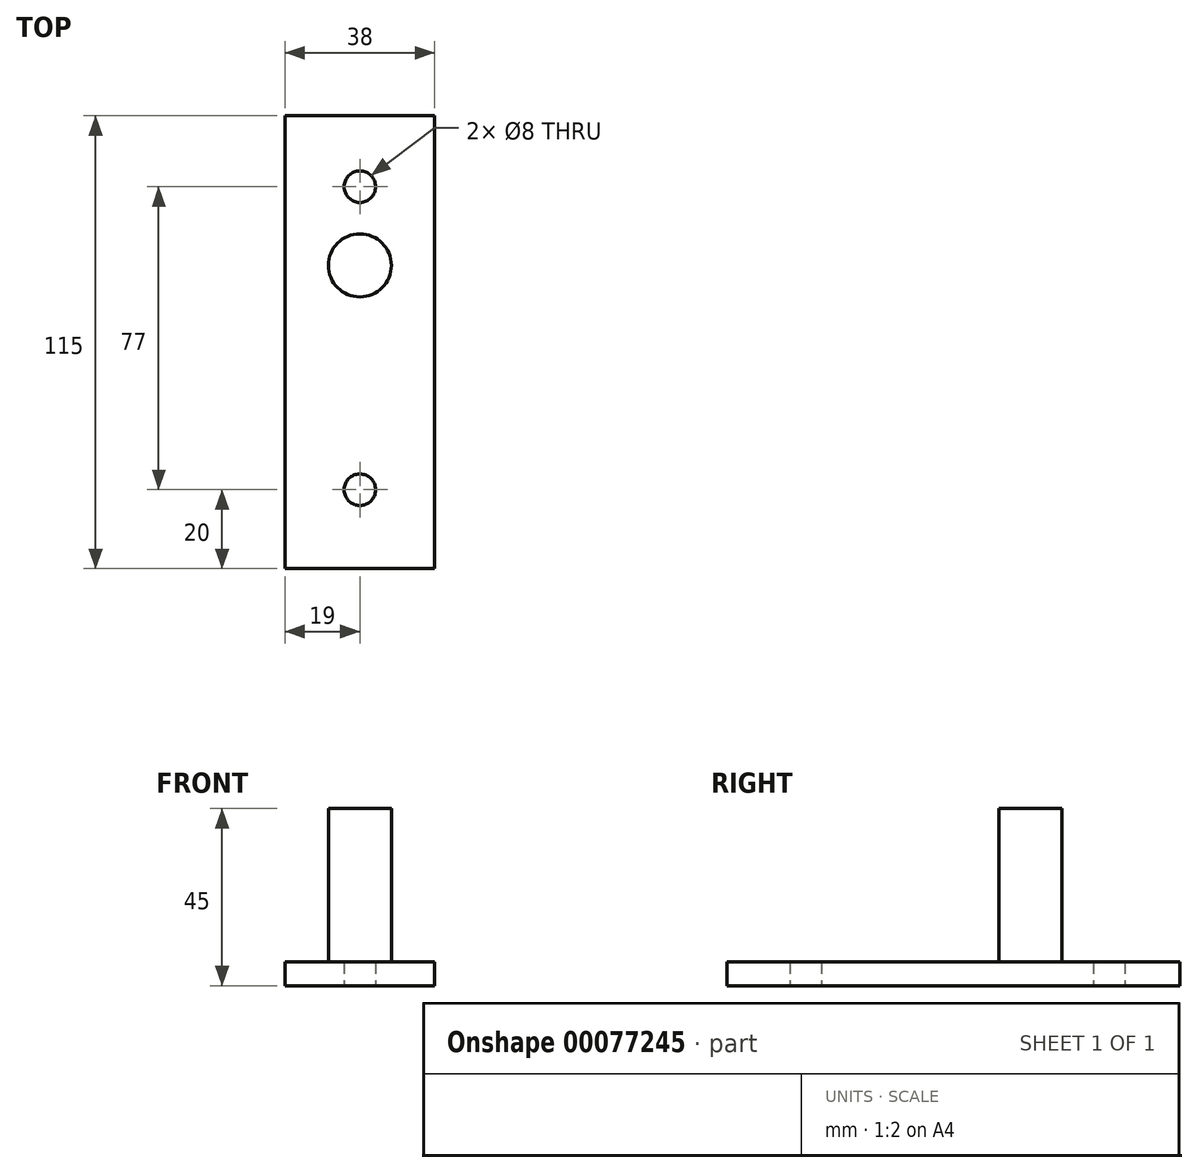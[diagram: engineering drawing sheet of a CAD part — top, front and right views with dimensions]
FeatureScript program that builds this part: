
annotation { "Feature Type Name" : "Feature", "Feature Type Description" : "" }
export const myFeature = defineFeature(function(context is Context, id is Id, definition is map)
    precondition{}
    {
        {
            var Q0;
            Q0=qCreatedBy(makeId("Top.planeOp"),FACE);
            var sketch = newSketch(context, id + "F0", { "sketchPlane" : qUnion([Q0])});
            skLineSegment(sketch, "E0", {"start": v(0, 57.5) * mm, "end": v(19, 57.5) * mm});
            skLineSegment(sketch, "E1", {"start": v(19, 57.5) * mm, "end": v(19, 0) * mm});
            skLineSegment(sketch, "E2.MirrorCS", {"start": v(0, 57.5) * mm, "end": v(-19, 57.5) * mm});
            skLineSegment(sketch, "E3.MirrorCS", {"start": v(-19, 57.5) * mm, "end": v(-19, 0) * mm});
            skLineSegment(sketch, "E4.MirrorCS", {"start": v(-19, -57.5) * mm, "end": v(-19, 0) * mm});
            skLineSegment(sketch, "E5.MirrorCS", {"start": v(19, -57.5) * mm, "end": v(19, 0) * mm});
            skLineSegment(sketch, "E6.MirrorCS", {"start": v(0, -57.5) * mm, "end": v(19, -57.5) * mm});
            skLineSegment(sketch, "E7.MirrorCS", {"start": v(0, -57.5) * mm, "end": v(-19, -57.5) * mm});
            skCircle(sketch, "E8", {"center": v(0, 19.5) * mm, "radius": 8 * mm});
            skPoint(sketch, "E9", {"position": v(0, 39.5) * mm});
            skPoint(sketch, "E10", {"position": v(0, -37.5) * mm});
            skSolve(sketch);
        }
        {
            var Q0;
            Q0 = qSketchRegion(id + "F0", true);
            var Q1;
            Q1=makeQuery(id+"F0.imprint","IMPRINT",FACE,{"disambiguationData":[TD([[makeQuery(id+"F0.imprint","IMPRINT",EDGE,{"derivedFrom":sQuery(id+"F0.wireOp",EDGE,"E8")}),1.0]])]});
            extrude(context, id + "F1", {"entities" : qUnion([Q0, Q1]), "depth" : 6 * mm});
        }
        {
            var Q0;
            Q0=makeQuery(id+"F0.imprint","IMPRINT",FACE,{"disambiguationData":[TD([[makeQuery(id+"F0.imprint","IMPRINT",EDGE,{"derivedFrom":sQuery(id+"F0.wireOp",EDGE,"E8")}),1.0]])]});
            extrude(context, id + "F2", {"entities" : qUnion([Q0]), "operationType" : NewBodyOperationType.ADD, "depth" : 45 * mm});
        }
        {
            var Q0;
            Q0=sQuery(id+"F0.wireOp",VERTEX,"E9");
            var Q1;
            Q1=sQuery(id+"F0.wireOp",VERTEX,"E10");
            var Q2;
            Q2=makeQuery(id+"F1.opExtrude","SWEPT_BODY",BODY,{"disambiguationData":[OSD([sQuery(id+"F0.wireOp",EDGE,"E0"),sQuery(id+"F0.wireOp",EDGE,"E1"),sQuery(id+"F0.wireOp",EDGE,"E2.MirrorCS"),sQuery(id+"F0.wireOp",EDGE,"E3.MirrorCS"),sQuery(id+"F0.wireOp",EDGE,"E4.MirrorCS"),sQuery(id+"F0.wireOp",EDGE,"E5.MirrorCS"),sQuery(id+"F0.wireOp",EDGE,"E6.MirrorCS"),sQuery(id+"F0.wireOp",EDGE,"E7.MirrorCS")])]});
            hole(context, id + "F3", {"style" : HoleStyle.SIMPLE, "endStyle" : HoleEndStyle.THROUGH, "oppositeDirection" : true, "holeDiameter" : 8 * mm, "locations" : qUnion([Q0, Q1]), "scope" : qUnion([Q2]), "isTappedThrough" : true});
        }
    });
